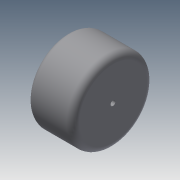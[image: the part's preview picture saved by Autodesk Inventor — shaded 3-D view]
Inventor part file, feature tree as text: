
AUTODESK INVENTOR PART (.ipt)
format: ipt  version: 2013 (Build 170138000, 138)  size: 115,712 bytes
history: native  units: mm
features: extrude x2, fillet x2, sketch x2
ambient origin geometry x8: Origin, YZ Plane, XZ Plane, XY Plane, X Axis, Y Axis, Z Axis, Center Point
bodies: Solid1 (feature_tree)
feature tree (6):
  extrude  "Extrusion1"  Depth=57.0mm TaperAngle=0.0deg
  extrude  "Extrusion2"  Depth=57.0mm TaperAngle=0.0deg
  fillet  "Fillet1"  Radius=8.0mm
  fillet  "Fillet2"  Radius=8.0mm
  sketch  "Sketch1"  dims[d0=100.0mm d1=57.0mm d2=0.0mm]
  sketch  "Sketch2"  dims[d3=6.0mm d4=57.0mm d5=0.0mm d6=8.0mm d7=8.0mm]
